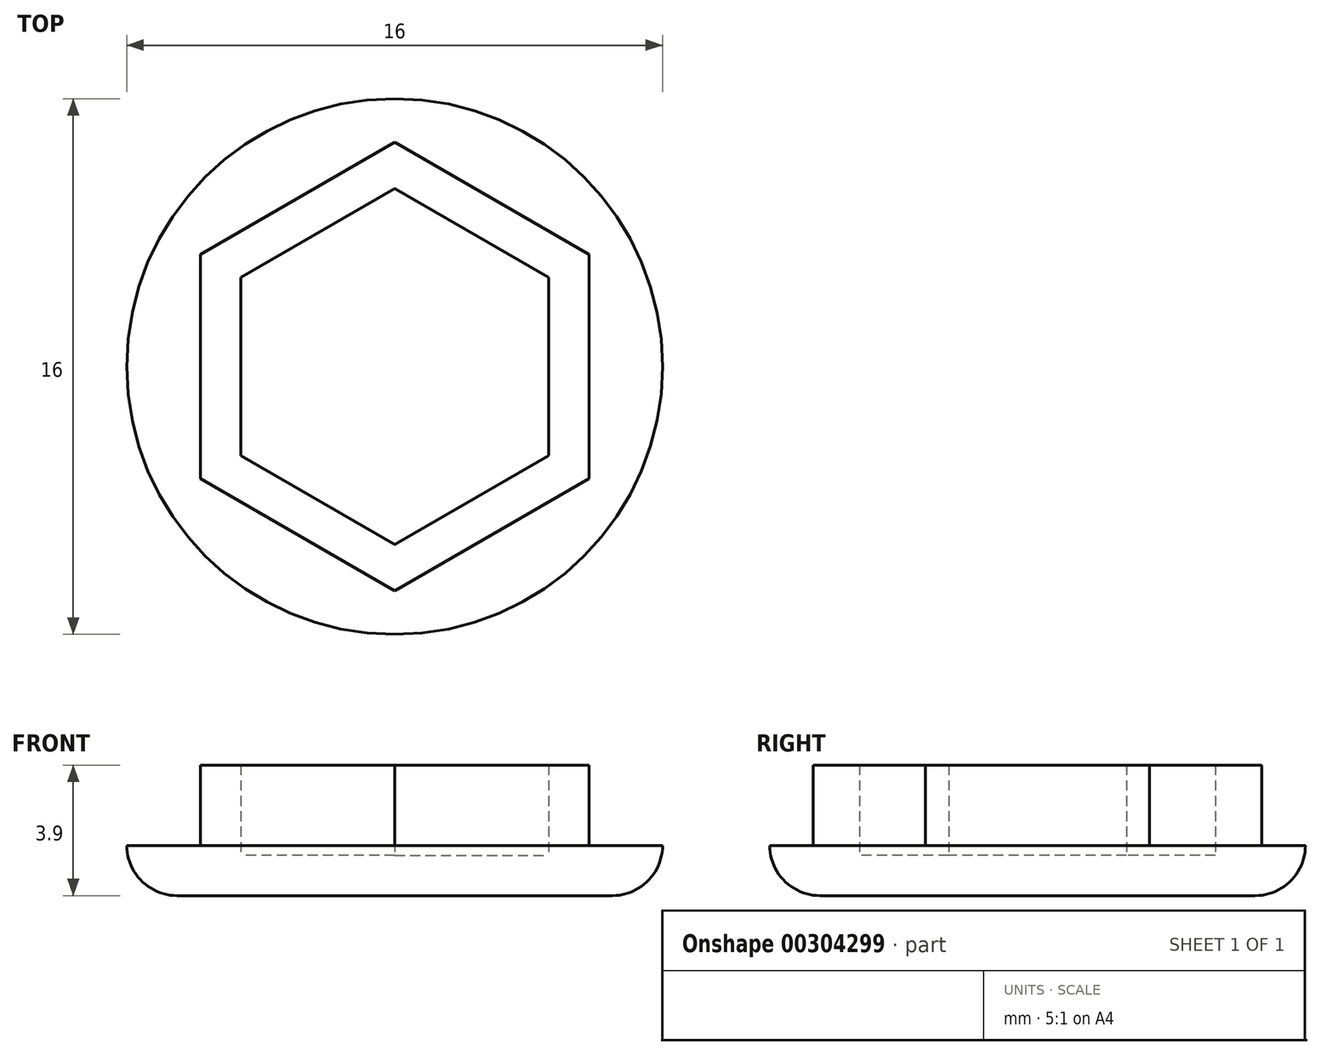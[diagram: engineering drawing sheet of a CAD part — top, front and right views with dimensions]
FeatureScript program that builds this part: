
annotation { "Feature Type Name" : "Feature", "Feature Type Description" : "" }
export const myFeature = defineFeature(function(context is Context, id is Id, definition is map)
    precondition{}
    {
        {
            var Q0;
            Q0=qCreatedBy(makeId("Top.planeOp"),FACE);
            var sketch = newSketch(context, id + "F0", { "sketchPlane" : qUnion([Q0])});
            skCircle(sketch, "E0", {"center": v(0, 0) * mm, "radius": 8 * mm});
            skSolve(sketch);
        }
        {
            var Q0;
            Q0=makeQuery(id+"F0.imprint","IMPRINT",FACE,{"disambiguationData":[TD([[makeQuery(id+"F0.imprint","IMPRINT",EDGE,{"derivedFrom":sQuery(id+"F0.wireOp",EDGE,"E0")}),1.0]])]});
            extrude(context, id + "F1", {"entities" : qUnion([Q0]), "depth" : 1.5 * mm});
        }
        {
            var Q0;
            Q0=makeQuery(id+"F1.opExtrude","CAP_FACE",FACE,{"disambiguationData":[OSD([sQuery(id+"F0.wireOp",EDGE,"E0")])],"isStart":false});
            var sketch = newSketch(context, id + "F2", { "sketchPlane" : qUnion([Q0])});
            skCircle(sketch, "E1.cCircle", {"center": v(0, 0) * mm, "radius": 5.8 * mm, "construction": true});
            skLineSegment(sketch, "E1.0", {"start": v(5.8, 3.35) * mm, "end": v(5.8, -3.35) * mm});
            skLineSegment(sketch, "E1.1", {"start": v(5.8, -3.35) * mm, "end": v(0, -6.7) * mm});
            skLineSegment(sketch, "E1.2", {"start": v(0, -6.7) * mm, "end": v(-5.8, -3.35) * mm});
            skLineSegment(sketch, "E1.3", {"start": v(-5.8, -3.35) * mm, "end": v(-5.8, 3.35) * mm});
            skLineSegment(sketch, "E1.4", {"start": v(-5.8, 3.35) * mm, "end": v(0, 6.7) * mm});
            skLineSegment(sketch, "E1.5", {"start": v(0, 6.7) * mm, "end": v(5.8, 3.35) * mm});
            skPoint(sketch, "E1.0.midPoint", {"position": v(5.8, 0) * mm});
            skSolve(sketch);
        }
        {
            var Q0;
            Q0=makeQuery(id+"F2.imprint","IMPRINT",FACE,{"disambiguationData":[TD([[makeQuery(id+"F2.imprint","IMPRINT",EDGE,{"derivedFrom":sQuery(id+"F2.wireOp",EDGE,"E1.0")}),-1.0]])]});
            extrude(context, id + "F3", {"entities" : qUnion([Q0]), "operationType" : NewBodyOperationType.ADD, "depth" : 2.4 * mm});
        }
        {
            var Q0;
            Q0=makeQuery(id+"F3.opExtrude","CAP_FACE",FACE,{"disambiguationData":[OSD([sQuery(id+"F2.wireOp",EDGE,"E1.0"),sQuery(id+"F2.wireOp",EDGE,"E1.1"),sQuery(id+"F2.wireOp",EDGE,"E1.2"),sQuery(id+"F2.wireOp",EDGE,"E1.3"),sQuery(id+"F2.wireOp",EDGE,"E1.4"),sQuery(id+"F2.wireOp",EDGE,"E1.5")])],"isStart":false});
            shell(context, id + "F4", {"entities" : qUnion([Q0]), "thickness" : 1.2 * mm});
        }
        {
            var Q0;
            Q0=makeQuery(id+"F1.opExtrude","CAP_EDGE",EDGE,{"disambiguationData":[OSD([sQuery(id+"F0.wireOp",EDGE,"E0")])],"isStart":true});
            fillet(context, id + "F5", {"entities" : qUnion([Q0]), "radius" : 1.5 * mm, "tangentPropagation" : true, "allowEdgeOverflow" : false});
        }
    });
